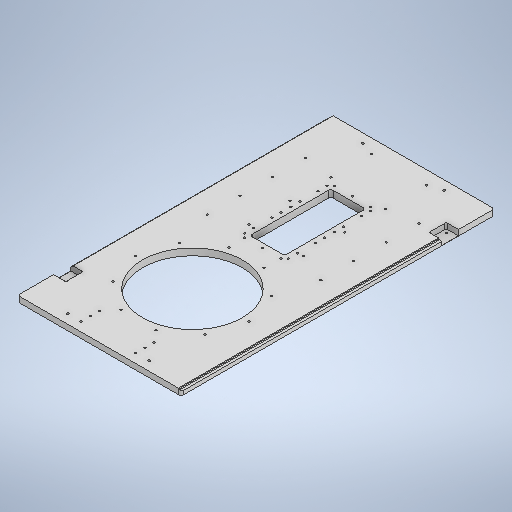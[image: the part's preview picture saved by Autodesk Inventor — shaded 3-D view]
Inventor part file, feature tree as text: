
AUTODESK INVENTOR PART (.ipt)
format: ipt  version: 2025 (Build 290162000, 162)  size: 571,392 bytes
history: native  units: in
note: dims shown in document units (in); Inventor stores cm internally (conversion verified against a paired STEP export)
features: sketch x17, extrude x6, hole x5, fillet x3, chamfer x3, plane x2
ambient origin geometry x8: Origin, YZ Plane, XZ Plane, XY Plane, X Axis, Y Axis, Z Axis, Center Point
bodies: Solid1 (feature_tree)
feature tree (36):
  extrude  "Base Cover"  Depth=27.1654in
  sketch  "Sketch2"  dims[d5=8.6614in d6=0.0in d7=0.0in]
  extrude  "Cylinder Hole"  Depth=0.5906in
  plane  "Work Plane1"
  hole  "Hole3"  [1 undecoded]
  sketch  "Sketch7"  dims[d69=0.1575in d70=3.937in d72=360.0deg]
  plane  "Work Plane2"
  hole  "Hole4"  [1 undecoded]
  sketch  "Sketch9"  dims[d82=1.063in]
  fillet  "Rounded Side Corners"  Radius=7.0625in
  chamfer  "Chamfer1"  Distance=3.937in Angle=360.0deg
  chamfer  "Chamfer2"  Distance=0.1969in
  extrude  "Magnet Seats"  Depth=0.3937in TaperAngle=45.0deg
  hole  "Hole5"  [1 undecoded]
  chamfer  "Chamfer5"  Distance=0.1181in
  hole  "Hole6"  [1 undecoded]
  sketch  "Sketch15"  dims[d85=1.4961in]
  extrude  "Extrusion11"  Depth=0.3937in TaperAngle=0.0deg
  fillet  "Fillet3"  Radius=0.748in
  hole  "Hole7"  [1 undecoded]
  fillet  "Rounded Bottom Corners"  Radius=0.8661in
  extrude  "Side Rail_L"  Depth=0.3937in
  extrude  "Side Rail_R"  Depth=0.3937in
  sketch  "Sketch1"  dims[d0=14.1732in d1=27.1654in]
  sketch  "Sketch6"  dims[d68=9.8425in]
  sketch  "Sketch8"  dims[d74=0.1628in d75=0.3937in d76=0.1575in d77=0.0787in d78=90.0deg d79=0.3937in d80=0.8108in]
  sketch  "Sketch Circular Pattern4"  dims[d57=0.1936in d58=0.1969in d59=0.1575in d60=0.0787in d61=90.0deg d62=0.1969in d63=0.8108in]
  sketch  "Sketch11"  dims[d83=1.063in]
  sketch  "Sketch12"  dims[d84=1.4961in]
  sketch  "Sketch Rectangular Pattern1"  dims[d2=0.5906in d3=0.0in d4=8.0709in]
  sketch  "Sketch Rectangular Pattern2"  dims[d8=10.6299in d50=5.9055in d55=7.0625in]
  sketch  "Sketch Rectangular Pattern3"  dims[d56=25.5906in]
  sketch  "Sketch Rectangular Pattern4"  dims[d64=10.3543in]
  sketch  "Sketch Rectangular Pattern5"  dims[d65=10.6299in]
  sketch  "Sketch16"  dims[d86=3.1102in]
  sketch  "Sketch17"  dims[d87=3.1102in d88=0.1969in d89=0.0984in d90=0.0787in d91=45.0deg d92=0.0984in d93=0.0787in d94=45.0deg d95=0.1181in d96=0.1181in d97=0.4724in d98=0.0in d109=0.748in d110=0.315in d111=0.8661in d112=0.748in d113=0.1299in d114=0.1299in d115=0.1299in d116=0.1299in d118=0.315in d119=0.8661in d120=0.748in d121=0.748in d122=0.1276in d123=0.315in d124=0.1575in d125=0.0787in d126=90.0deg d127=0.315in d128=0.8108in d129=0.0138in d130=0.0787in d131=45.0deg d146=3.9469in d147=0.7874in d148=0.3937in d149=0.1575in d150=3.937in d152=1.1811in d153=0.3937in d155=0.3937in d157=0.1575in d158=1.1811in d160=0.7874in d161=0.3937in d163=0.3937in d165=9.8425in d166=0.1575in d167=2.9528in d168=1.1811in d169=3.1496in d171=1.4173in d172=0.3937in d174=0.3937in d176=0.1628in d177=0.3937in d178=0.1575in d179=0.0787in d180=90.0deg d181=0.3937in d182=0.8108in d191=3.0in d192=7.0in d193=6.4961in d194=0.8312in d195=0.0in d196=0.1969in d197=0.3937in d198=0.1969in d199=1.9685in d201=0.7874in d202=0.3937in d204=0.3937in d206=0.3189in d207=0.1969in d208=0.3189in d209=1.9685in d211=0.7874in d212=0.3937in d214=0.3937in d216=0.1628in d217=0.3937in d218=0.1575in d219=0.0787in d220=90.0deg d221=0.3937in d222=0.8108in d230=0.2756in d231=0.2362in d232=0.0787in d233=0.1378in d234=0.503in d235=0.5906in d236=0.0in d237=0.1378in d238=0.0787in d239=0.2362in d240=0.503in d241=0.3937in d242=0.0in d26=0.0394in d27=0.0394in d28=0.0394in d29=0.0059in d30=0.0098in d31=0.0148in d32=0.5635in d33=0.0295in d34=0.8108in d35=0.0025in d36=0.0295in d37=0.0148in d66=0.0197in d67=0.0344in]
note: 5 required parameter values undecoded (feature->parameter linkage not recoverable at this tier; creation-order binding heuristic only, values carry confidence <= 0.55)
